# Revit family: Tap-Sink Set-Caroma G Series Exposed Breech 80 Lever (160 Outlet)-Wall_Temp_5dd0f7b9-14f0-4afa-8b5f-f429eaa61fbc
name_source: partatom
category: Plumbing Fixtures
revit_build: Autodesk Revit 2015 (Build: 20160512_1515(x64)
units: mm (PartAtom-declared; Revit-internal decimal feet)

## types (1)
- Chrome
    Assembly Code = D2020
    CW Connection = Yes
    CWFU = 0
    ColdWaterConnectorDiameter = 20 mm  [stored 0.0656168 ft]
    Cost = 0 $
    Default Elevation = 1000 mm  [stored 3.28084 ft]
    Description = WELS 4 star rated, 7.5L/min
    HW Connection = Yes
    HWFU = 0
    HotWaterConnectorDiameter = 20 mm  [stored 0.0656168 ft]
    Manufacturer = GWA Bathrooms&Kitchens
    Material_ANZRS = Metal-Chrome-Caroma
    Model = G53380C4A
    ModifiedIssue_ANZRS = 20170419.54 $
    Type Comments = Caroma G Series Plus Exp Breech Wall Set 160 outlet 80 Hdl
    URL = http://specify.caroma.com.au
    Vent Connection = No
    Waste Connection = No

note: [stored X ft] marks values corroborated as IEEE doubles in the binary element streams (Revit-internal decimal feet)

## geometry (parser evidence)
native form markers: Sweep x2
no freeform markers — native parametric forms only
